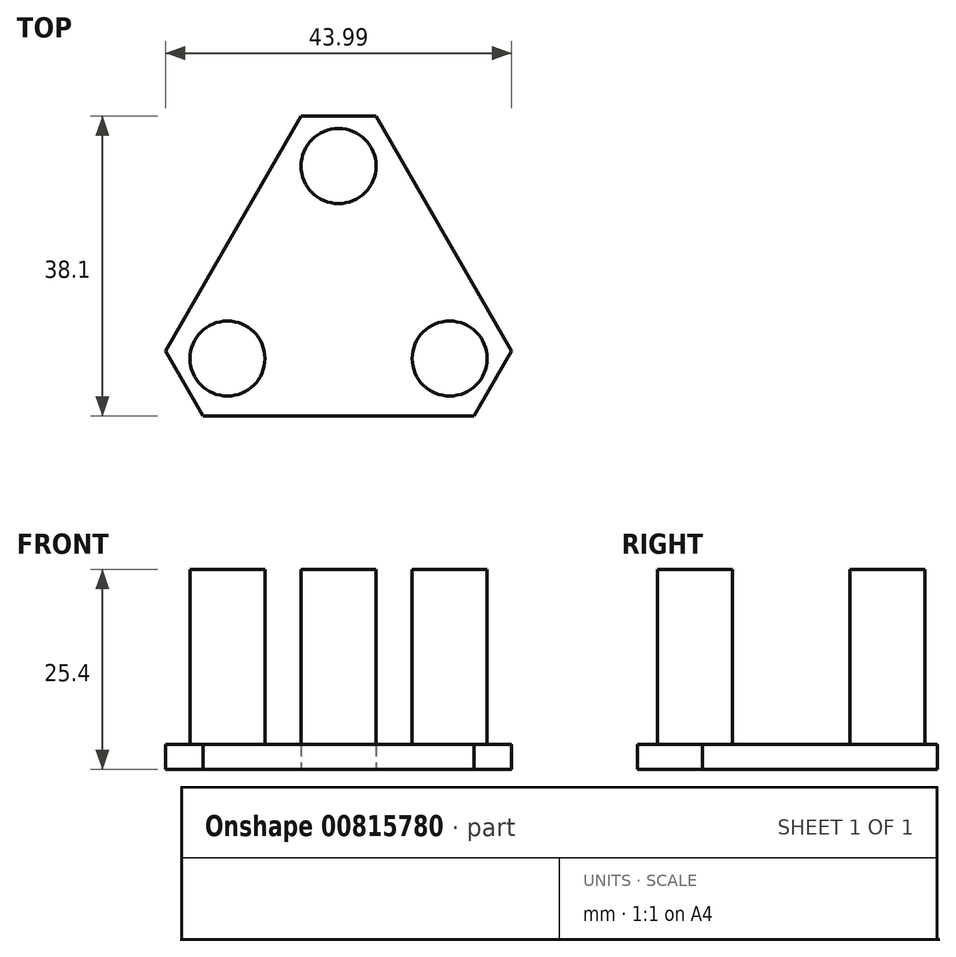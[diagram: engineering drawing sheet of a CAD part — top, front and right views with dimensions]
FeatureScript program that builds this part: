
annotation { "Feature Type Name" : "Feature", "Feature Type Description" : "" }
export const myFeature = defineFeature(function(context is Context, id is Id, definition is map)
    precondition{}
    {
        {
            var Q0;
            Q0=qCreatedBy(makeId("Top.planeOp"),FACE);
            var sketch = newSketch(context, id + "F0", { "sketchPlane" : qUnion([Q0])});
            skLineSegment(sketch, "E0", {"start": v(0, 0) * mm, "end": v(17.23, 29.85) * mm});
            skLineSegment(sketch, "E1", {"start": v(17.23, 29.85) * mm, "end": v(26.76, 29.85) * mm});
            skLineSegment(sketch, "E2", {"start": v(26.76, 29.85) * mm, "end": v(44, 0) * mm});
            skLineSegment(sketch, "E3", {"start": v(44, 0) * mm, "end": v(39.23, -8.25) * mm});
            skLineSegment(sketch, "E4", {"start": v(39.23, -8.25) * mm, "end": v(4.76, -8.25) * mm});
            skLineSegment(sketch, "E5", {"start": v(4.76, -8.25) * mm, "end": v(0, 0) * mm});
            skLineSegment(sketch, "E6", {"start": v(22, -8.25) * mm, "end": v(22, 29.85) * mm, "construction": true});
            skCircle(sketch, "E7", {"center": v(22, 23.5) * mm, "radius": 4.76 * mm});
            skCircle(sketch, "E8", {"center": v(36.11, -0.95) * mm, "radius": 4.76 * mm});
            skCircle(sketch, "E9", {"center": v(7.88, -0.95) * mm, "radius": 4.76 * mm});
            skLineSegment(sketch, "E10", {"start": v(2.38, -4.12) * mm, "end": v(7.88, -0.95) * mm});
            skSolve(sketch);
        }
        {
            var Q0;
            Q0 = qSketchRegion(id + "F0", true);
            var Q1;
            Q1=makeQuery(id+"F0.imprint","IMPRINT",FACE,{"disambiguationData":[TD([[makeQuery(id+"F0.imprint","IMPRINT",EDGE,{"derivedFrom":sQuery(id+"F0.wireOp",EDGE,"E7")}),1.0]])]});
            var Q2;
            Q2=makeQuery(id+"F0.imprint","IMPRINT",FACE,{"disambiguationData":[TD([[makeQuery(id+"F0.imprint","IMPRINT",EDGE,{"derivedFrom":sQuery(id+"F0.wireOp",EDGE,"E9")}),1.0]])]});
            var Q3;
            Q3=makeQuery(id+"F0.imprint","IMPRINT",FACE,{"disambiguationData":[TD([[makeQuery(id+"F0.imprint","IMPRINT",EDGE,{"derivedFrom":sQuery(id+"F0.wireOp",EDGE,"E8")}),1.0]])]});
            extrude(context, id + "F1", {"entities" : qUnion([Q0, Q1, Q2, Q3]), "depth" : 3.17 * mm, "offsetDistance" : 25.4 * mm});
        }
        {
            var Q0;
            Q0=makeQuery(id+"F0.imprint","IMPRINT",FACE,{"disambiguationData":[TD([[makeQuery(id+"F0.imprint","IMPRINT",EDGE,{"derivedFrom":sQuery(id+"F0.wireOp",EDGE,"E7")}),1.0]])]});
            var Q1;
            Q1=makeQuery(id+"F0.imprint","IMPRINT",FACE,{"disambiguationData":[TD([[makeQuery(id+"F0.imprint","IMPRINT",EDGE,{"derivedFrom":sQuery(id+"F0.wireOp",EDGE,"E8")}),1.0]])]});
            var Q2;
            Q2=makeQuery(id+"F0.imprint","IMPRINT",FACE,{"disambiguationData":[TD([[makeQuery(id+"F0.imprint","IMPRINT",EDGE,{"derivedFrom":sQuery(id+"F0.wireOp",EDGE,"E9")}),1.0]])]});
            extrude(context, id + "F2", {"entities" : qUnion([Q0, Q1, Q2]), "operationType" : NewBodyOperationType.ADD, "depth" : 25.4 * mm, "offsetDistance" : 25.4 * mm});
        }
    });
